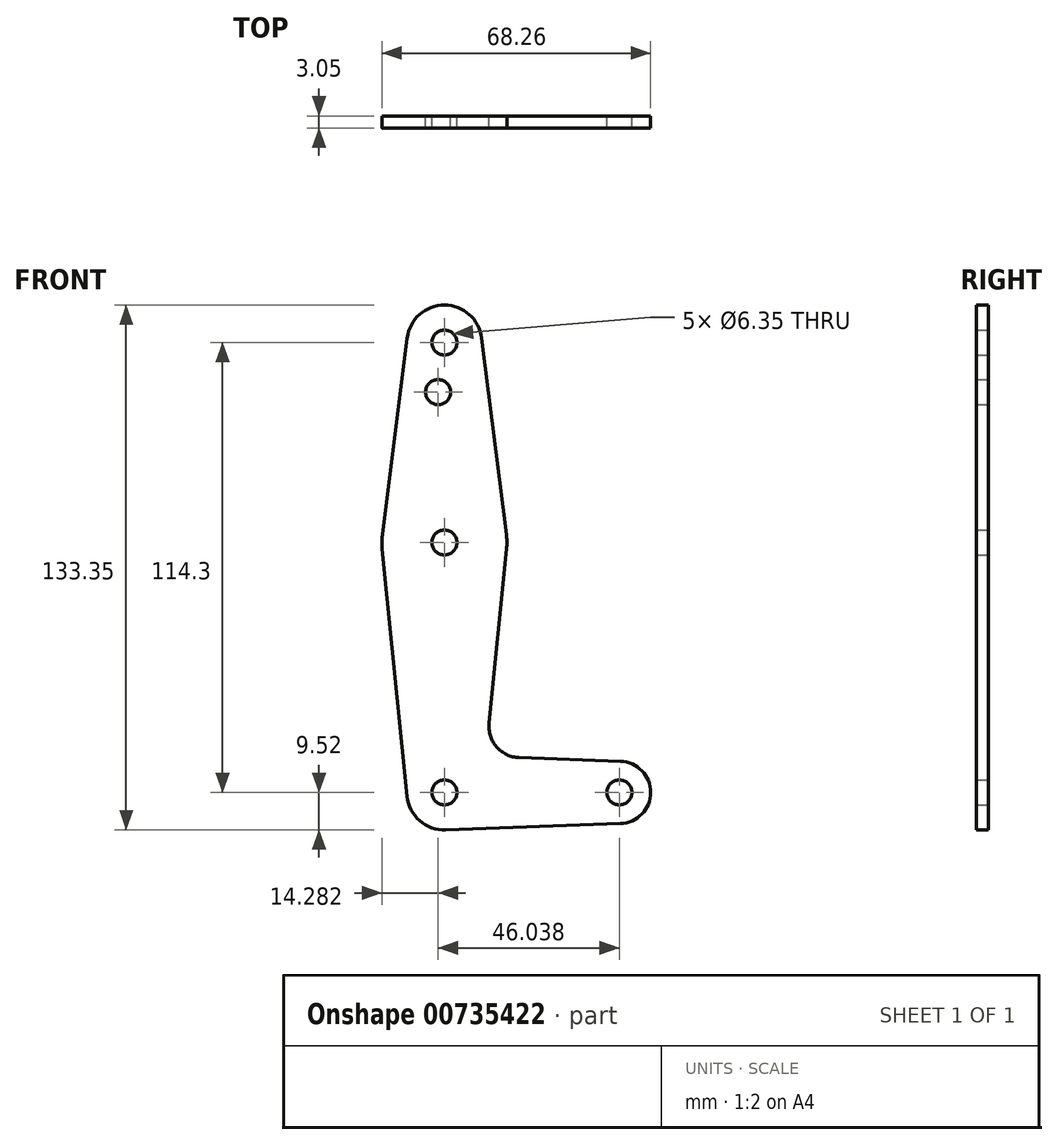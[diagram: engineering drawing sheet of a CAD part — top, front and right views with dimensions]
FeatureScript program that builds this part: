
annotation { "Feature Type Name" : "Feature", "Feature Type Description" : "" }
export const myFeature = defineFeature(function(context is Context, id is Id, definition is map)
    precondition{}
    {
        {
            var Q0;
            Q0=qCreatedBy(makeId("Front.planeOp"),FACE);
            var sketch = newSketch(context, id + "F0", { "sketchPlane" : qUnion([Q0])});
            skLineSegment(sketch, "E0", {"start": v(0, 0) * mm, "end": v(0, 114.3) * mm, "construction": true});
            skLineSegment(sketch, "E1", {"start": v(0, 0) * mm, "end": v(44.45, 0) * mm, "construction": true});
            skCircle(sketch, "E2", {"center": v(0, 114.3) * mm, "radius": 9.53 * mm});
            skCircle(sketch, "E3", {"center": v(0, 63.5) * mm, "radius": 15.88 * mm});
            skCircle(sketch, "E4", {"center": v(0, 0) * mm, "radius": 9.53 * mm});
            skCircle(sketch, "E5", {"center": v(44.45, 0) * mm, "radius": 7.94 * mm});
            skLineSegment(sketch, "E6", {"start": v(-9.45, 115.5) * mm, "end": v(-15.75, 65.48) * mm});
            skLineSegment(sketch, "E7", {"start": v(9.45, 115.5) * mm, "end": v(15.75, 65.48) * mm});
            skLineSegment(sketch, "E8", {"start": v(-15.8, 61.91) * mm, "end": v(-9.48, -0.95) * mm});
            skLineSegment(sketch, "E9", {"start": v(15.8, 61.91) * mm, "end": v(11.34, 17.6) * mm});
            skLineSegment(sketch, "E10", {"start": v(18.97, 8.85) * mm, "end": v(44.73, 7.93) * mm});
            skLineSegment(sketch, "E11", {"start": v(0.34, -9.52) * mm, "end": v(44.73, -7.93) * mm});
            skCircle(sketch, "E12", {"center": v(0, 114.3) * mm, "radius": 3.18 * mm});
            skCircle(sketch, "E13", {"center": v(0, 63.5) * mm, "radius": 3.18 * mm});
            skCircle(sketch, "E14", {"center": v(44.45, 0) * mm, "radius": 3.18 * mm});
            skCircle(sketch, "E15", {"center": v(-1.59, 101.7) * mm, "radius": 3.18 * mm});
            skCircle(sketch, "E16", {"center": v(0, 0) * mm, "radius": 3.18 * mm});
            skArc(sketch, "E17.filletArc", {"start": v(11.34, 17.6) * mm, "mid": v(13.26, 11.57) * mm, "end": v(18.97, 8.85) * mm});
            skSolve(sketch);
        }
        {
            var Q0;
            Q0 = qSketchRegion(id + "F0", true);
            extrude(context, id + "F1", {"entities" : qUnion([Q0]), "depth" : 3.05 * mm, "offsetDistance" : 25.4 * mm});
        }
    });
